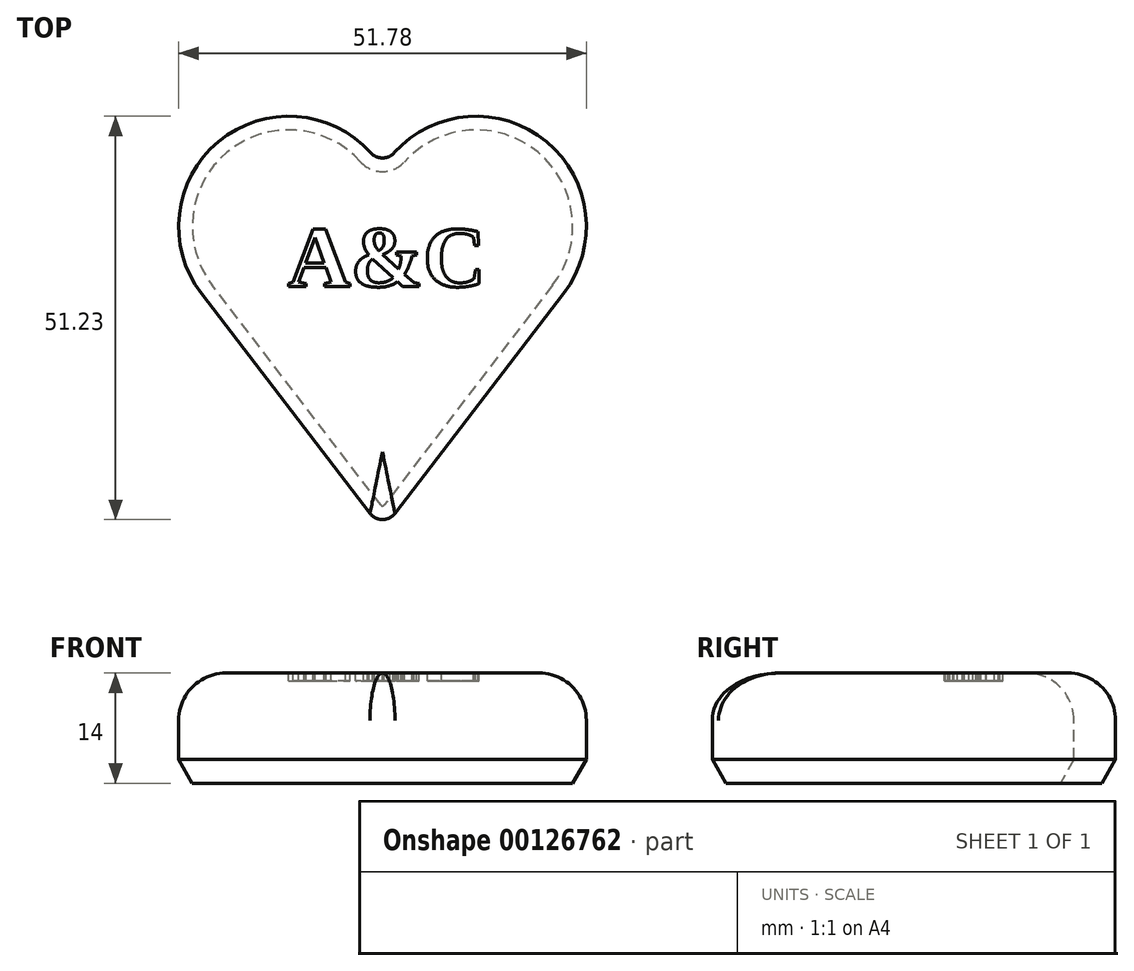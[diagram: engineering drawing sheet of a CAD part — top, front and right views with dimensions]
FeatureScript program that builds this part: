
annotation { "Feature Type Name" : "Feature", "Feature Type Description" : "" }
export const myFeature = defineFeature(function(context is Context, id is Id, definition is map)
    precondition{}
    {
        {
            var Q0;
            Q0=qCreatedBy(makeId("Top.planeOp"),FACE);
            var sketch = newSketch(context, id + "F0", { "sketchPlane" : qUnion([Q0])});
            skLineSegment(sketch, "E0", {"start": v(-23, 0) * mm, "end": v(0, -30) * mm});
            skLineSegment(sketch, "E1", {"start": v(0, -30) * mm, "end": v(23, 0) * mm});
            skArc(sketch, "E2", {"start": v(23, 0) * mm, "mid": v(19.85, 20.03) * mm, "end": v(0, 15.9) * mm});
            skArc(sketch, "E3", {"start": v(-23, 0) * mm, "mid": v(-19.85, 20.03) * mm, "end": v(0, 15.9) * mm});
            skSolve(sketch);
        }
        {
            var Q0;
            Q0 = qSketchRegion(id + "F0", true);
            extrude(context, id + "F1", {"entities" : qUnion([Q0]), "depth" : 14 * mm});
        }
        {
            var Q0;
            Q0=makeQuery(id+"F1.opExtrude","SWEPT_EDGE",EDGE,{"disambiguationData":[OSD([sQuery(id+"F0.wireOp",EDGE,"E0"),sQuery(id+"F0.wireOp",EDGE,"E1")])]});
            var Q1;
            Q1=makeQuery(id+"F1.opExtrude","SWEPT_EDGE",EDGE,{"disambiguationData":[OSD([sQuery(id+"F0.wireOp",EDGE,"E2"),sQuery(id+"F0.wireOp",EDGE,"E3")])]});
            fillet(context, id + "F2", {"entities" : qUnion([Q0, Q1]), "radius" : 2 * mm, "tangentPropagation" : true, "allowEdgeOverflow" : false});
        }
        {
            var Q0;
            Q0=makeQuery(id+"F1.opExtrude","CAP_EDGE",EDGE,{"disambiguationData":[OSD([sQuery(id+"F0.wireOp",EDGE,"E1")])],"isStart":false});
            fillet(context, id + "F3", {"entities" : qUnion([Q0]), "radius" : 6 * mm, "tangentPropagation" : true, "allowEdgeOverflow" : false});
        }
        {
            var Q0;
            Q0=makeQuery(id+"F1.opExtrude","CAP_EDGE",EDGE,{"disambiguationData":[OSD([sQuery(id+"F0.wireOp",EDGE,"E0")])],"isStart":true});
            chamfer(context, id + "F4", {"entities" : qUnion([Q0]), "chamferType" : ChamferType.OFFSET_ANGLE, "width" : 3 * mm, "oppositeDirection" : false, "angle" : 30 * degree, "tangentPropagation" : true});
        }
        {
            var Q0;
            Q0=makeQuery(id+"F1.opExtrude","CAP_FACE",FACE,{"disambiguationData":[OSD([sQuery(id+"F0.wireOp",EDGE,"E0"),sQuery(id+"F0.wireOp",EDGE,"E1"),sQuery(id+"F0.wireOp",EDGE,"E2"),sQuery(id+"F0.wireOp",EDGE,"E3")])],"isStart":false});
            var sketch = newSketch(context, id + "F5", { "sketchPlane" : qUnion([Q0])});
            skText(sketch, "E4", { "text": "A&C", "fontName": "Tinos-Bold.ttf"});
            const initialGuessF5  = {"E4": [-0.01202, 0.0009, 1, 0, 0.00795]};
            skSetInitialGuess(sketch, initialGuessF5);
            skSolve(sketch);
        }
        {
            var Q0;
            Q0 = qSketchRegion(id + "F5", true);
            extrude(context, id + "F6", {"entities" : qUnion([Q0]), "operationType" : NewBodyOperationType.REMOVE, "oppositeDirection" : true, "depth" : 1 * mm});
        }
    });
